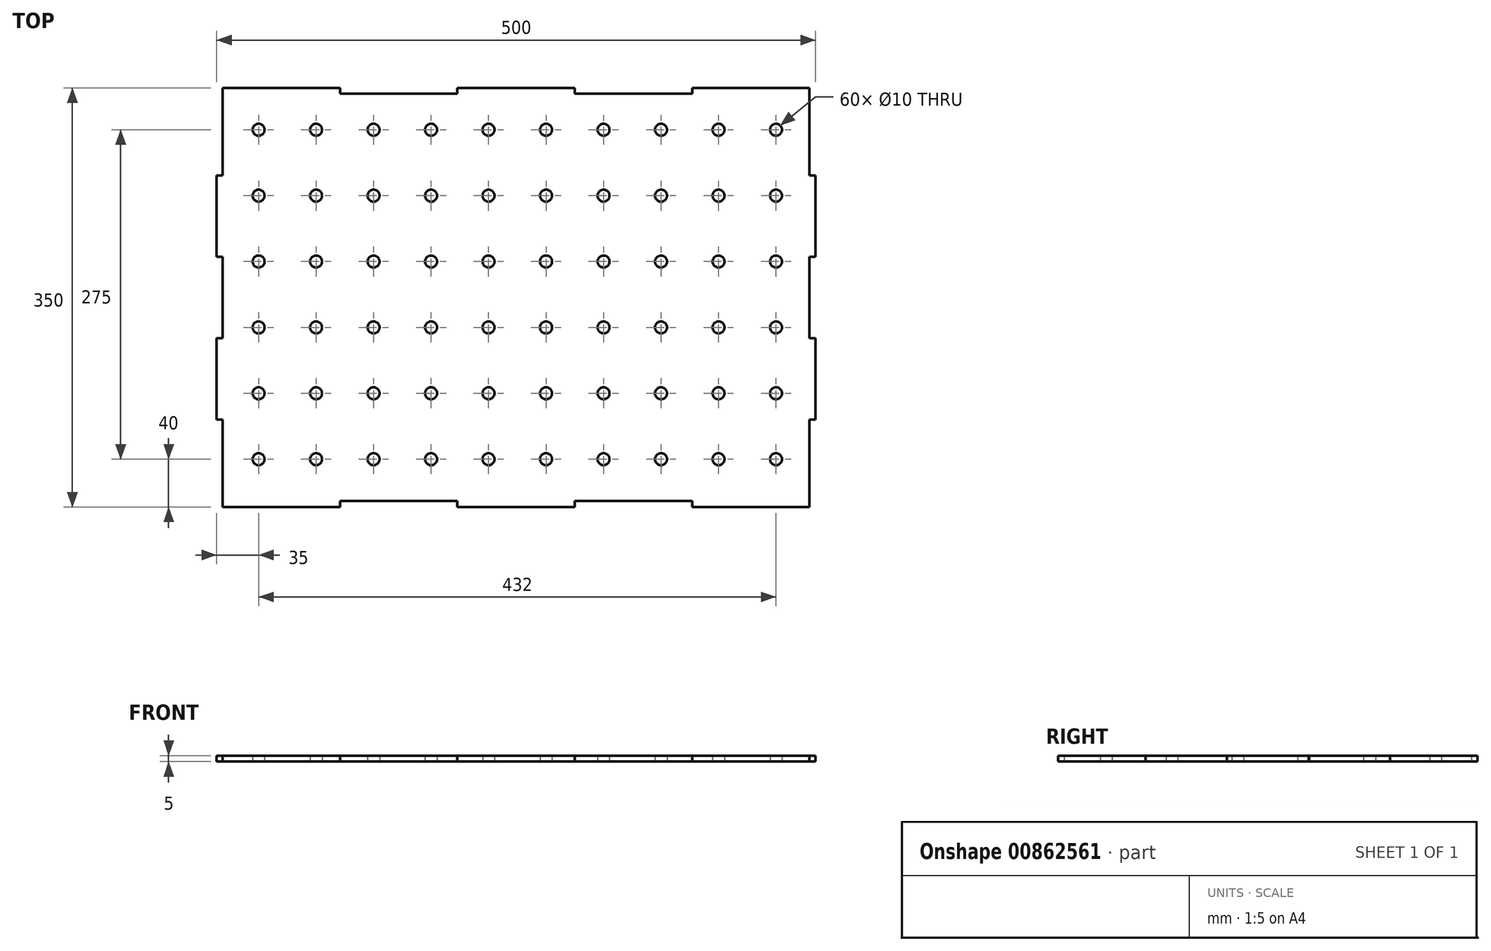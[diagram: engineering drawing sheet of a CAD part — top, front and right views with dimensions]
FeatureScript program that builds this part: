
annotation { "Feature Type Name" : "Feature", "Feature Type Description" : "" }
export const myFeature = defineFeature(function(context is Context, id is Id, definition is map)
    precondition{}
    {
        {
            var Q0;
            Q0=qCreatedBy(makeId("Top.planeOp"),FACE);
            var sketch = newSketch(context, id + "F0", { "sketchPlane" : qUnion([Q0])});
            skLineSegment(sketch, "E0.bottom", {"start": v(245, -170) * mm, "end": v(-245, -170) * mm});
            skLineSegment(sketch, "E0.top", {"start": v(245, 170) * mm, "end": v(-245, 170) * mm});
            skLineSegment(sketch, "E0.left", {"start": v(245, -170) * mm, "end": v(245, 170) * mm});
            skLineSegment(sketch, "E0.right", {"start": v(-245, -170) * mm, "end": v(-245, 170) * mm});
            skPoint(sketch, "E0.middle", {"position": v(0, 0) * mm});
            skLineSegment(sketch, "E1", {"start": v(-245, -170) * mm, "end": v(-245, -175) * mm});
            skLineSegment(sketch, "E2", {"start": v(-245, -175) * mm, "end": v(-147, -175) * mm});
            skLineSegment(sketch, "E3", {"start": v(-147, -175) * mm, "end": v(-147, -170) * mm});
            skLineSegment(sketch, "E4", {"start": v(-552.17, 0) * mm, "end": v(393.12, 0) * mm});
            skLineSegment(sketch, "E5", {"start": v(0, -308.05) * mm, "end": v(0, 300.63) * mm});
            skLineSegment(sketch, "E6.MirrorCS", {"start": v(-245, 170) * mm, "end": v(-245, 175) * mm});
            skLineSegment(sketch, "E7.MirrorCS", {"start": v(-245, 175) * mm, "end": v(-147, 175) * mm});
            skLineSegment(sketch, "E8.MirrorCS", {"start": v(-147, 175) * mm, "end": v(-147, 170) * mm});
            skLineSegment(sketch, "E9.1.0.0", {"start": v(-49, 170) * mm, "end": v(-49, 175) * mm});
            skLineSegment(sketch, "E9.1.0.1", {"start": v(-49, 175) * mm, "end": v(49, 175) * mm});
            skLineSegment(sketch, "E9.1.0.2", {"start": v(49, 175) * mm, "end": v(49, 170) * mm});
            skLineSegment(sketch, "E9.1.0.3", {"start": v(-49, -170) * mm, "end": v(-49, -175) * mm});
            skLineSegment(sketch, "E9.1.0.4", {"start": v(-49, -175) * mm, "end": v(49, -175) * mm});
            skLineSegment(sketch, "E9.1.0.5", {"start": v(49, -175) * mm, "end": v(49, -170) * mm});
            skLineSegment(sketch, "E9.2.0.0", {"start": v(147, 170) * mm, "end": v(147, 175) * mm});
            skLineSegment(sketch, "E9.2.0.1", {"start": v(147, 175) * mm, "end": v(245, 175) * mm});
            skLineSegment(sketch, "E9.2.0.2", {"start": v(245, 175) * mm, "end": v(245, 170) * mm});
            skLineSegment(sketch, "E9.2.0.3", {"start": v(147, -170) * mm, "end": v(147, -175) * mm});
            skLineSegment(sketch, "E9.2.0.4", {"start": v(147, -175) * mm, "end": v(245, -175) * mm});
            skLineSegment(sketch, "E9.2.0.5", {"start": v(245, -175) * mm, "end": v(245, -170) * mm});
            skLineSegment(sketch, "E9.direction1", {"start": v(-245, 170) * mm, "end": v(-49, 170) * mm, "construction": true});
            skLineSegment(sketch, "E10", {"start": v(245, 102) * mm, "end": v(250, 102) * mm});
            skLineSegment(sketch, "E11", {"start": v(250, 102) * mm, "end": v(250, 34) * mm});
            skLineSegment(sketch, "E12", {"start": v(250, 34) * mm, "end": v(245, 34) * mm});
            skLineSegment(sketch, "E13.MirrorCS", {"start": v(-245, 102) * mm, "end": v(-250, 102) * mm});
            skLineSegment(sketch, "E14.MirrorCS", {"start": v(-250, 102) * mm, "end": v(-250, 34) * mm});
            skLineSegment(sketch, "E15.MirrorCS", {"start": v(-250, 34) * mm, "end": v(-245, 34) * mm});
            skLineSegment(sketch, "E16.MirrorCS", {"start": v(-245, -102) * mm, "end": v(-250, -102) * mm});
            skLineSegment(sketch, "E17.MirrorCS", {"start": v(-250, -102) * mm, "end": v(-250, -34) * mm});
            skLineSegment(sketch, "E18.MirrorCS", {"start": v(-250, -34) * mm, "end": v(-245, -34) * mm});
            skLineSegment(sketch, "E19.MirrorCS", {"start": v(245, -102) * mm, "end": v(250, -102) * mm});
            skLineSegment(sketch, "E20.MirrorCS", {"start": v(250, -102) * mm, "end": v(250, -34) * mm});
            skLineSegment(sketch, "E21.MirrorCS", {"start": v(250, -34) * mm, "end": v(245, -34) * mm});
            skCircle(sketch, "E22", {"center": v(-215, 140) * mm, "radius": 5 * mm});
            skCircle(sketch, "E23.0.1.0", {"center": v(-215, 85) * mm, "radius": 5 * mm});
            skCircle(sketch, "E23.0.2.0", {"center": v(-215, 30) * mm, "radius": 5 * mm});
            skCircle(sketch, "E23.0.3.0", {"center": v(-215, -25) * mm, "radius": 5 * mm});
            skCircle(sketch, "E23.0.4.0", {"center": v(-215, -80) * mm, "radius": 5 * mm});
            skCircle(sketch, "E23.0.5.0", {"center": v(-215, -135) * mm, "radius": 5 * mm});
            skCircle(sketch, "E23.1.0.0", {"center": v(-167, 140) * mm, "radius": 5 * mm});
            skCircle(sketch, "E23.1.1.0", {"center": v(-167, 85) * mm, "radius": 5 * mm});
            skCircle(sketch, "E23.1.2.0", {"center": v(-167, 30) * mm, "radius": 5 * mm});
            skCircle(sketch, "E23.1.3.0", {"center": v(-167, -25) * mm, "radius": 5 * mm});
            skCircle(sketch, "E23.1.4.0", {"center": v(-167, -80) * mm, "radius": 5 * mm});
            skCircle(sketch, "E23.1.5.0", {"center": v(-167, -135) * mm, "radius": 5 * mm});
            skCircle(sketch, "E23.2.0.0", {"center": v(-119, 140) * mm, "radius": 5 * mm});
            skCircle(sketch, "E23.2.1.0", {"center": v(-119, 85) * mm, "radius": 5 * mm});
            skCircle(sketch, "E23.2.2.0", {"center": v(-119, 30) * mm, "radius": 5 * mm});
            skCircle(sketch, "E23.2.3.0", {"center": v(-119, -25) * mm, "radius": 5 * mm});
            skCircle(sketch, "E23.2.4.0", {"center": v(-119, -80) * mm, "radius": 5 * mm});
            skCircle(sketch, "E23.2.5.0", {"center": v(-119, -135) * mm, "radius": 5 * mm});
            skCircle(sketch, "E23.3.0.0", {"center": v(-71, 140) * mm, "radius": 5 * mm});
            skCircle(sketch, "E23.3.1.0", {"center": v(-71, 85) * mm, "radius": 5 * mm});
            skCircle(sketch, "E23.3.2.0", {"center": v(-71, 30) * mm, "radius": 5 * mm});
            skCircle(sketch, "E23.3.3.0", {"center": v(-71, -25) * mm, "radius": 5 * mm});
            skCircle(sketch, "E23.3.4.0", {"center": v(-71, -80) * mm, "radius": 5 * mm});
            skCircle(sketch, "E23.3.5.0", {"center": v(-71, -135) * mm, "radius": 5 * mm});
            skCircle(sketch, "E23.4.0.0", {"center": v(-23, 140) * mm, "radius": 5 * mm});
            skCircle(sketch, "E23.4.1.0", {"center": v(-23, 85) * mm, "radius": 5 * mm});
            skCircle(sketch, "E23.4.2.0", {"center": v(-23, 30) * mm, "radius": 5 * mm});
            skCircle(sketch, "E23.4.3.0", {"center": v(-23, -25) * mm, "radius": 5 * mm});
            skCircle(sketch, "E23.4.4.0", {"center": v(-23, -80) * mm, "radius": 5 * mm});
            skCircle(sketch, "E23.4.5.0", {"center": v(-23, -135) * mm, "radius": 5 * mm});
            skCircle(sketch, "E23.5.0.0", {"center": v(25, 140) * mm, "radius": 5 * mm});
            skCircle(sketch, "E23.5.1.0", {"center": v(25, 85) * mm, "radius": 5 * mm});
            skCircle(sketch, "E23.5.2.0", {"center": v(25, 30) * mm, "radius": 5 * mm});
            skCircle(sketch, "E23.5.3.0", {"center": v(25, -25) * mm, "radius": 5 * mm});
            skCircle(sketch, "E23.5.4.0", {"center": v(25, -80) * mm, "radius": 5 * mm});
            skCircle(sketch, "E23.5.5.0", {"center": v(25, -135) * mm, "radius": 5 * mm});
            skCircle(sketch, "E23.6.0.0", {"center": v(73, 140) * mm, "radius": 5 * mm});
            skCircle(sketch, "E23.6.1.0", {"center": v(73, 85) * mm, "radius": 5 * mm});
            skCircle(sketch, "E23.6.2.0", {"center": v(73, 30) * mm, "radius": 5 * mm});
            skCircle(sketch, "E23.6.3.0", {"center": v(73, -25) * mm, "radius": 5 * mm});
            skCircle(sketch, "E23.6.4.0", {"center": v(73, -80) * mm, "radius": 5 * mm});
            skCircle(sketch, "E23.6.5.0", {"center": v(73, -135) * mm, "radius": 5 * mm});
            skCircle(sketch, "E23.7.0.0", {"center": v(121, 140) * mm, "radius": 5 * mm});
            skCircle(sketch, "E23.7.1.0", {"center": v(121, 85) * mm, "radius": 5 * mm});
            skCircle(sketch, "E23.7.2.0", {"center": v(121, 30) * mm, "radius": 5 * mm});
            skCircle(sketch, "E23.7.3.0", {"center": v(121, -25) * mm, "radius": 5 * mm});
            skCircle(sketch, "E23.7.4.0", {"center": v(121, -80) * mm, "radius": 5 * mm});
            skCircle(sketch, "E23.7.5.0", {"center": v(121, -135) * mm, "radius": 5 * mm});
            skCircle(sketch, "E23.8.0.0", {"center": v(169, 140) * mm, "radius": 5 * mm});
            skCircle(sketch, "E23.8.1.0", {"center": v(169, 85) * mm, "radius": 5 * mm});
            skCircle(sketch, "E23.8.2.0", {"center": v(169, 30) * mm, "radius": 5 * mm});
            skCircle(sketch, "E23.8.3.0", {"center": v(169, -25) * mm, "radius": 5 * mm});
            skCircle(sketch, "E23.8.4.0", {"center": v(169, -80) * mm, "radius": 5 * mm});
            skCircle(sketch, "E23.8.5.0", {"center": v(169, -135) * mm, "radius": 5 * mm});
            skCircle(sketch, "E23.9.0.0", {"center": v(217, 140) * mm, "radius": 5 * mm});
            skCircle(sketch, "E23.9.1.0", {"center": v(217, 85) * mm, "radius": 5 * mm});
            skCircle(sketch, "E23.9.2.0", {"center": v(217, 30) * mm, "radius": 5 * mm});
            skCircle(sketch, "E23.9.3.0", {"center": v(217, -25) * mm, "radius": 5 * mm});
            skCircle(sketch, "E23.9.4.0", {"center": v(217, -80) * mm, "radius": 5 * mm});
            skCircle(sketch, "E23.9.5.0", {"center": v(217, -135) * mm, "radius": 5 * mm});
            skLineSegment(sketch, "E23.direction1", {"start": v(-215, 140) * mm, "end": v(-167, 140) * mm, "construction": true});
            skLineSegment(sketch, "E23.direction2", {"start": v(-215, 140) * mm, "end": v(-215, 85) * mm, "construction": true});
            skSolve(sketch);
        }
        {
            var Q0;
            Q0 = qSketchRegion(id + "F0", true);
            extrude(context, id + "F1", {"entities" : qUnion([Q0]), "depth" : 5 * mm, "offsetDistance" : 25 * mm});
        }
    });
